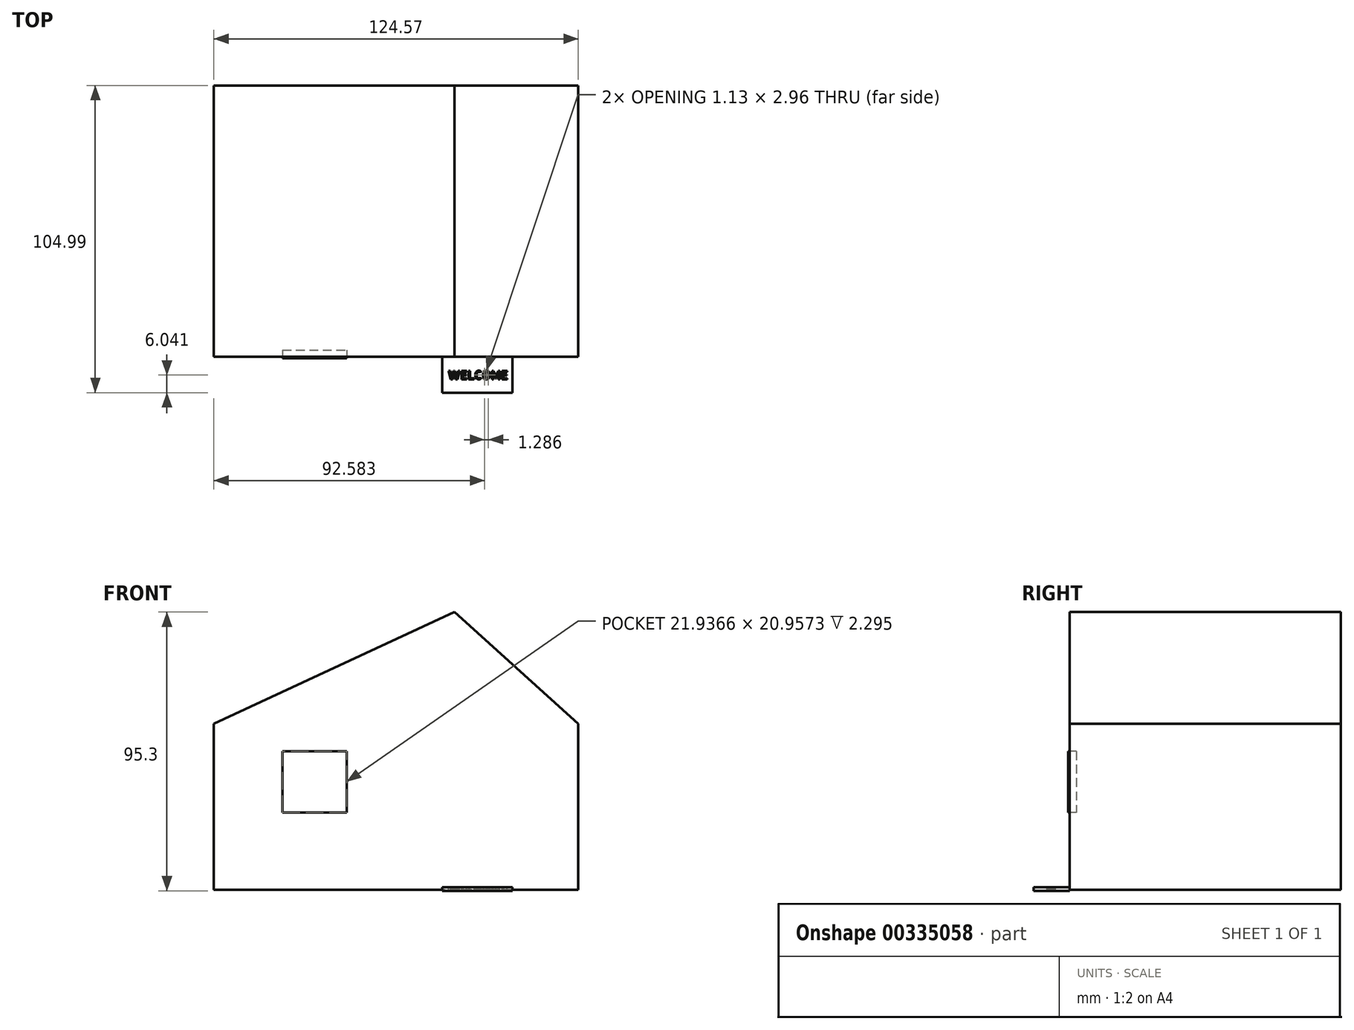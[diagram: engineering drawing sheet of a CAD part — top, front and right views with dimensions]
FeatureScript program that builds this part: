
annotation { "Feature Type Name" : "Feature", "Feature Type Description" : "" }
export const myFeature = defineFeature(function(context is Context, id is Id, definition is map)
    precondition{}
    {
        {
            var Q0;
            Q0=qCreatedBy(makeId("Front.planeOp"),FACE);
            var sketch = newSketch(context, id + "F0", { "sketchPlane" : qUnion([Q0])});
            skLineSegment(sketch, "E0.bottom", {"start": v(-56.21, 22.82) * mm, "end": v(68.36, 22.82) * mm});
            skLineSegment(sketch, "E0.top", {"start": v(-56.21, -33.98) * mm, "end": v(68.36, -33.98) * mm});
            skLineSegment(sketch, "E0.left", {"start": v(-56.21, 22.82) * mm, "end": v(-56.21, -33.98) * mm});
            skLineSegment(sketch, "E0.right", {"start": v(68.36, 22.82) * mm, "end": v(68.36, -33.98) * mm});
            skLineSegment(sketch, "E1", {"start": v(-56.21, 22.82) * mm, "end": v(26.05, 61.01) * mm});
            skLineSegment(sketch, "E2", {"start": v(26.05, 61.01) * mm, "end": v(68.36, 22.82) * mm});
            skSolve(sketch);
        }
        {
            var Q0;
            Q0=makeQuery(id+"F0.imprint","IMPRINT",FACE,{"disambiguationData":[TD([[makeQuery(id+"F0.imprint","IMPRINT",EDGE,{"derivedFrom":sQuery(id+"F0.wireOp",EDGE,"E0.bottom")}),1.0]])]});
            var Q1;
            Q1=makeQuery(id+"F0.imprint","IMPRINT",FACE,{"disambiguationData":[TD([[makeQuery(id+"F0.imprint","IMPRINT",EDGE,{"derivedFrom":sQuery(id+"F0.wireOp",EDGE,"E0.bottom")}),-1.0]])]});
            extrude(context, id + "F1", {"entities" : qUnion([Q0, Q1]), "endBound" : BoundingType.SYMMETRIC, "depth" : 92.66 * mm});
        }
        {
            var Q0;
            Q0=qCreatedBy(makeId("Top.planeOp"),FACE);
            var sketch = newSketch(context, id + "F2", { "sketchPlane" : qUnion([Q0])});
            skLineSegment(sketch, "E3.bottom", {"start": v(21.94, -46.32) * mm, "end": v(45.83, -46.32) * mm});
            skLineSegment(sketch, "E3.top", {"start": v(21.94, -58.66) * mm, "end": v(45.83, -58.66) * mm});
            skLineSegment(sketch, "E3.left", {"start": v(21.94, -46.32) * mm, "end": v(21.94, -58.66) * mm});
            skLineSegment(sketch, "E3.right", {"start": v(45.83, -46.32) * mm, "end": v(45.83, -58.66) * mm});
            skSolve(sketch);
        }
        {
            var Q0;
            Q0=qSketchRegion(id+"F2",true);
            extrude(context, id + "F3", {"entities" : qUnion([Q0]), "depth" : 1.22 * mm});
        }
        {
            var Q0;
            Q0=makeQuery(id+"F3.opExtrude","SWEPT_BODY",BODY,{"disambiguationData":[OSD([sQuery(id+"F2.wireOp",EDGE,"E3.bottom"),sQuery(id+"F2.wireOp",EDGE,"E3.top"),sQuery(id+"F2.wireOp",EDGE,"E3.left"),sQuery(id+"F2.wireOp",EDGE,"E3.right")])]});
            var Q1;
            Q1=qCreatedBy(makeId("Top.planeOp"),FACE);
            transform(context, id + "F4", {"entities" : qUnion([Q0]), "transformType" : TransformType.TRANSLATION_DISTANCE, "transformDirection" : qUnion([Q1]), "distance" : 34.3 * mm, "oppositeDirection" : true, "makeCopy" : false});
        }
        {
            var Q0;
            Q0=qCreatedBy(makeId("Top.planeOp"),FACE);
            var sketch = newSketch(context, id + "F5", { "sketchPlane" : qUnion([Q0])});
            skText(sketch, "E4", { "text": "WELCOME", "fontName": "AllertaStencil-Regular.ttf"});
            const initialGuessF5  = {"E4": [0.0238, -0.05408, 1, 0, 0.0029]};
            skSetInitialGuess(sketch, initialGuessF5);
            skSolve(sketch);
        }
        {
            var Q0;
            Q0=qSketchRegion(id+"F5",true);
            extrude(context, id + "F6", {"entities" : qUnion([Q0]), "operationType" : NewBodyOperationType.REMOVE, "oppositeDirection" : true, "depth" : 34.43 * mm});
        }
        {
            var Q0;
            Q0=makeQuery(id+"F1.opExtrude","CAP_FACE",FACE,{"disambiguationData":[OSD([sQuery(id+"F0.wireOp",EDGE,"E0.top"),sQuery(id+"F0.wireOp",EDGE,"E0.left"),sQuery(id+"F0.wireOp",EDGE,"E0.right"),sQuery(id+"F0.wireOp",EDGE,"E1"),sQuery(id+"F0.wireOp",EDGE,"E2")])],"isStart":false});
            var sketch = newSketch(context, id + "F7", { "sketchPlane" : qUnion([Q0])});
            skLineSegment(sketch, "E5.bottom", {"start": v(18.41, 4.4) * mm, "end": v(48.97, 4.4) * mm});
            skLineSegment(sketch, "E5.top", {"start": v(18.41, -33.98) * mm, "end": v(48.97, -33.98) * mm});
            skLineSegment(sketch, "E5.left", {"start": v(18.41, 4.4) * mm, "end": v(18.41, -33.98) * mm});
            skLineSegment(sketch, "E5.right", {"start": v(48.97, 4.4) * mm, "end": v(48.97, -33.98) * mm});
            skSolve(sketch);
        }
        {
            var Q0;
            Q0=makeQuery(id+"F7.imprint","IMPRINT",FACE,{"disambiguationData":[TD([[makeQuery(id+"F7.imprint","IMPRINT",EDGE,{"derivedFrom":sQuery(id+"F7.wireOp",EDGE,"E5.bottom")}),-1.0]])]});
            extrude(context, id + "F8", {"entities" : qUnion([Q0]), "operationType" : NewBodyOperationType.REMOVE, "oppositeDirection" : true, "depth" : 1.56 * mm});
        }
        {
            var Q0;
            Q0=makeQuery(id+"F1.opExtrude","CAP_FACE",FACE,{"disambiguationData":[OSD([sQuery(id+"F0.wireOp",EDGE,"E0.top"),sQuery(id+"F0.wireOp",EDGE,"E0.left"),sQuery(id+"F0.wireOp",EDGE,"E0.right"),sQuery(id+"F0.wireOp",EDGE,"E1"),sQuery(id+"F0.wireOp",EDGE,"E2")])],"isStart":false});
            var sketch = newSketch(context, id + "F9", { "sketchPlane" : qUnion([Q0])});
            skLineSegment(sketch, "E6.bottom", {"start": v(18.41, 4.4) * mm, "end": v(48.97, 4.4) * mm});
            skLineSegment(sketch, "E6.top", {"start": v(18.41, -33.98) * mm, "end": v(48.97, -33.98) * mm});
            skLineSegment(sketch, "E6.left", {"start": v(18.41, 4.4) * mm, "end": v(18.41, -33.98) * mm});
            skLineSegment(sketch, "E6.right", {"start": v(48.97, 4.4) * mm, "end": v(48.97, -33.98) * mm});
            skSolve(sketch);
        }
        {
            var Q0;
            Q0=makeQuery(id+"F9.imprint","IMPRINT",FACE,{"disambiguationData":[TD([[makeQuery(id+"F9.imprint","IMPRINT",EDGE,{"derivedFrom":sQuery(id+"F9.wireOp",EDGE,"E6.bottom")}),-1.0]])]});
            extrude(context, id + "F10", {"entities" : qUnion([Q0]), "operationType" : NewBodyOperationType.ADD, "oppositeDirection" : true, "depth" : 2.07 * mm});
        }
        {
            var Q0;
            Q0=makeQuery(id+"F1.opExtrude","CAP_FACE",FACE,{"disambiguationData":[OSD([sQuery(id+"F0.wireOp",EDGE,"E0.top"),sQuery(id+"F0.wireOp",EDGE,"E0.left"),sQuery(id+"F0.wireOp",EDGE,"E0.right"),sQuery(id+"F0.wireOp",EDGE,"E1"),sQuery(id+"F0.wireOp",EDGE,"E2")])],"isStart":false});
            var sketch = newSketch(context, id + "F11", { "sketchPlane" : qUnion([Q0])});
            skLineSegment(sketch, "E7.bottom", {"start": v(-32.7, 13.42) * mm, "end": v(-10.77, 13.42) * mm});
            skLineSegment(sketch, "E7.top", {"start": v(-32.7, -7.54) * mm, "end": v(-10.77, -7.54) * mm});
            skLineSegment(sketch, "E7.left", {"start": v(-32.7, 13.42) * mm, "end": v(-32.7, -7.54) * mm});
            skLineSegment(sketch, "E7.right", {"start": v(-10.77, 13.42) * mm, "end": v(-10.77, -7.54) * mm});
            skSolve(sketch);
        }
        {
            var Q0;
            Q0=makeQuery(id+"F11.imprint","IMPRINT",FACE,{"disambiguationData":[TD([[makeQuery(id+"F11.imprint","IMPRINT",EDGE,{"derivedFrom":sQuery(id+"F11.wireOp",EDGE,"E7.bottom")}),-1.0]])]});
            extrude(context, id + "F12", {"entities" : qUnion([Q0]), "operationType" : NewBodyOperationType.REMOVE, "oppositeDirection" : true, "depth" : 2.3 * mm});
        }
        {
            var Q0;
            Q0=makeQuery(id+"F1.opExtrude","CAP_FACE",FACE,{"disambiguationData":[OSD([sQuery(id+"F0.wireOp",EDGE,"E0.top"),sQuery(id+"F0.wireOp",EDGE,"E0.left"),sQuery(id+"F0.wireOp",EDGE,"E0.right"),sQuery(id+"F0.wireOp",EDGE,"E1"),sQuery(id+"F0.wireOp",EDGE,"E2")])],"isStart":false});
            var sketch = newSketch(context, id + "F13", { "sketchPlane" : qUnion([Q0])});
            skLineSegment(sketch, "E8.bottom", {"start": v(-32.7, 13.42) * mm, "end": v(-10.77, 13.42) * mm});
            skLineSegment(sketch, "E8.top", {"start": v(-32.7, -7.54) * mm, "end": v(-10.77, -7.54) * mm});
            skLineSegment(sketch, "E8.left", {"start": v(-32.7, 13.42) * mm, "end": v(-32.7, -7.54) * mm});
            skLineSegment(sketch, "E8.right", {"start": v(-10.77, 13.42) * mm, "end": v(-10.77, -7.54) * mm});
            skSolve(sketch);
        }
        {
            var Q0;
            Q0=makeQuery(id+"F13.imprint","IMPRINT",FACE,{"disambiguationData":[TD([[makeQuery(id+"F13.imprint","IMPRINT",EDGE,{"derivedFrom":sQuery(id+"F13.wireOp",EDGE,"E8.bottom")}),-1.0]])]});
            extrude(context, id + "F14", {"entities" : qUnion([Q0]), "operationType" : NewBodyOperationType.ADD, "depth" : 0.53 * mm});
        }
    });
